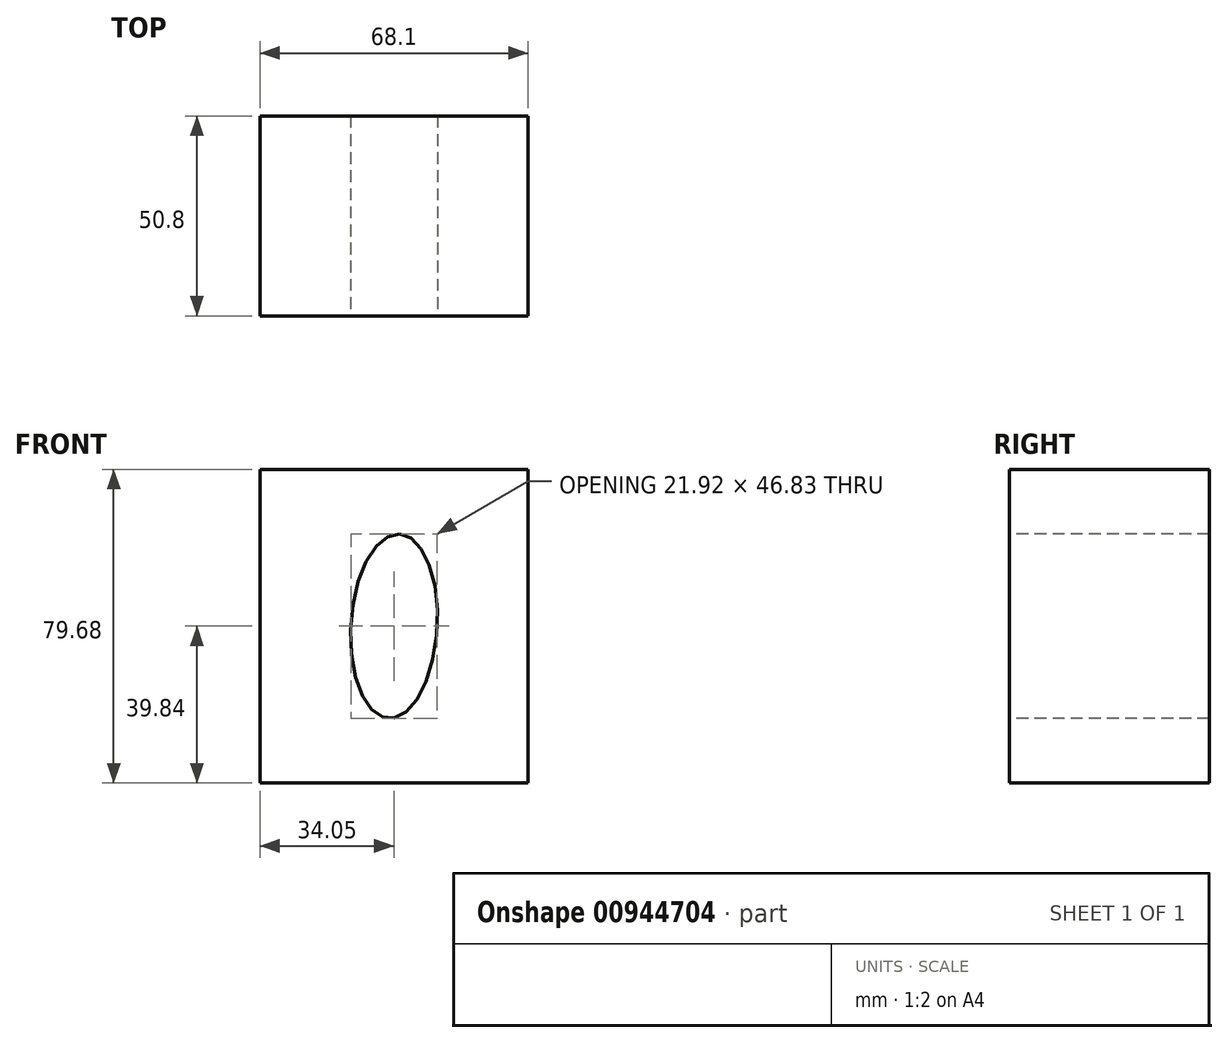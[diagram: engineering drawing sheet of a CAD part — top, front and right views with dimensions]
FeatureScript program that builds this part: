
annotation { "Feature Type Name" : "Feature", "Feature Type Description" : "" }
export const myFeature = defineFeature(function(context is Context, id is Id, definition is map)
    precondition{}
    {
        {
            var Q0;
            Q0=qCreatedBy(makeId("Front.planeOp"),FACE);
            var sketch = newSketch(context, id + "F0", { "sketchPlane" : qUnion([Q0])});
            skLineSegment(sketch, "E0.bottom", {"start": v(34.05, 39.84) * mm, "end": v(-34.05, 39.84) * mm});
            skLineSegment(sketch, "E0.top", {"start": v(34.05, -39.84) * mm, "end": v(-34.05, -39.84) * mm});
            skLineSegment(sketch, "E0.left", {"start": v(34.05, 39.84) * mm, "end": v(34.05, -39.84) * mm});
            skLineSegment(sketch, "E0.right", {"start": v(-34.05, 39.84) * mm, "end": v(-34.05, -39.84) * mm});
            skPoint(sketch, "E0.middle", {"position": v(0, 0) * mm});
            skSolve(sketch);
        }
        {
            var Q0;
            Q0 = qSketchRegion(id + "F0", true);
            extrude(context, id + "F1", {"entities" : qUnion([Q0]), "depth" : 50.8 * mm, "offsetDistance" : 25.4 * mm});
        }
        {
            var Q0;
            Q0=makeQuery(id+"F1.opExtrude","CAP_FACE",FACE,{"disambiguationData":[OSD([sQuery(id+"F0.wireOp",EDGE,"E0.bottom"),sQuery(id+"F0.wireOp",EDGE,"E0.top"),sQuery(id+"F0.wireOp",EDGE,"E0.left"),sQuery(id+"F0.wireOp",EDGE,"E0.right")])],"isStart":false});
            var sketch = newSketch(context, id + "F2", { "sketchPlane" : qUnion([Q0])});
            skEllipse(sketch, "E1", {"center": v(0, 0) * mm, "majorRadius": 23.46 * mm, "minorRadius": 10.98 * mm, "majorAxis": v(0.06, 1)});
            skSolve(sketch);
        }
        {
            var Q0;
            Q0 = qSketchRegion(id + "F2", true);
            extrude(context, id + "F3", {"entities" : qUnion([Q0]), "operationType" : NewBodyOperationType.REMOVE, "endBound" : BoundingType.UP_TO_NEXT, "oppositeDirection" : true, "depth" : 25.4 * mm, "offsetDistance" : 25.4 * mm});
        }
    });
